# Revit family: 22M MT 60 Fixed
name_source: partatom
category: Furniture
revit_build: Autodesk Revit 2016 (Build: 20150220_1215(x64)
units: mm (PartAtom-declared; Revit-internal decimal feet)

## family parameters
Always vertical = Yes
Cut with Voids When Loaded = No
OmniClass Number = 23.40.20.00
OmniClass Title = General Furniture and Specialties
Room Calculation Point = No
Shared = No
Work Plane-Based = No

## types (8) — shared parameters

## per-type parameters (varying)
| type | Height | Model | Shape |
| 22M MT Round 27" High 60" Size | 2' - 3" | 22M132760RD-MT | 22M 60 Round |
| 22M MT Elongated 27" High 60" Size | 2' - 3" | 22M132760EL-MT | 22M 60 Elongated |
| 22M MT Hex 27" High 60" Size | 2' - 3" | 22M132760HX-MT | 22M 60 Hex |
| 22M MT Square 27" High 60" Size | 2' - 3" | 22M132760SQ-MT | 22M 60 Square |
| 22M MT Square 29" High 60" Size | 2' - 5" | 22M132960SQ-MT | 22M 60 Square |
| 22M MT Round 29" High 60" Size | 2' - 5" | 22M132960RD-MT | 22M 60 Round |
| 22M MT Hex 29" High 60" Size | 2' - 5" | 22M132960HX-MT | 22M 60 Hex |
| 22M MT Elongated 29" High 60" Size | 2' - 5" | 22M132960EL-MT | 22M 60 Elongated |

## geometry (parser evidence)
native form markers: Sweep x10
no freeform markers — native parametric forms only
